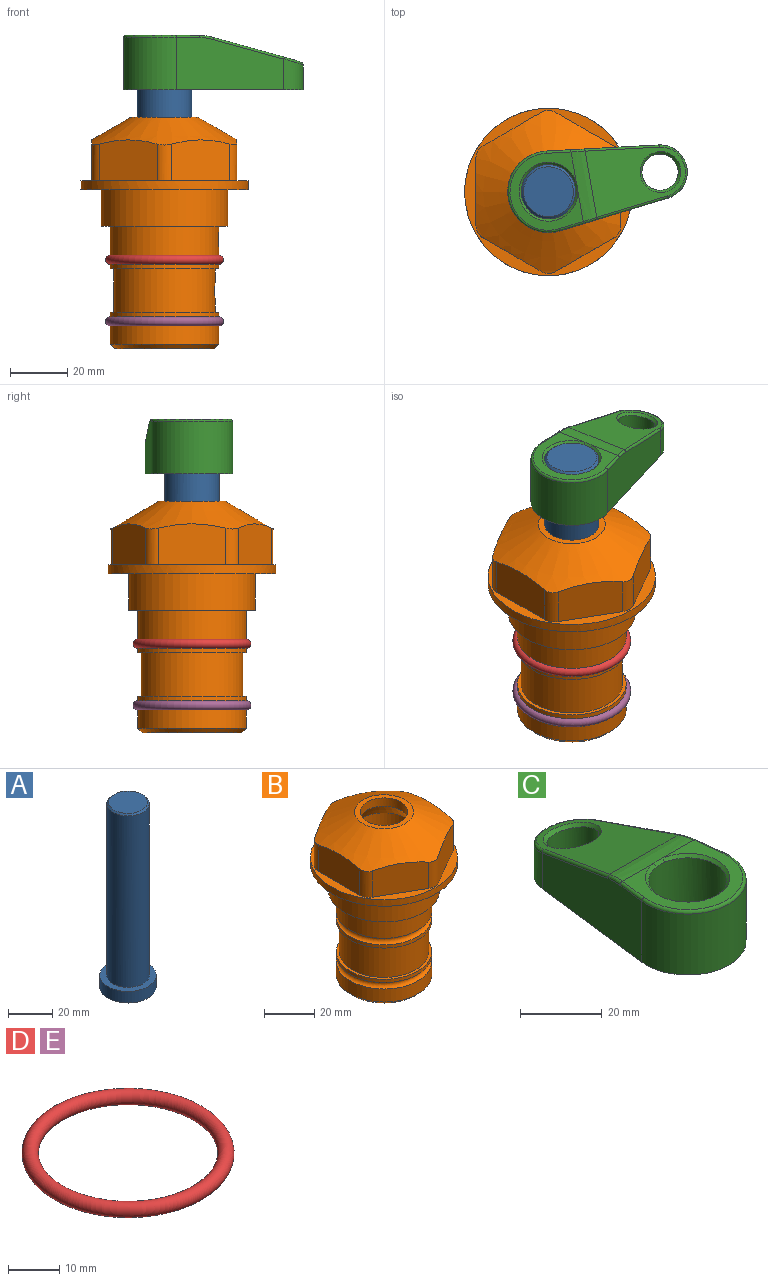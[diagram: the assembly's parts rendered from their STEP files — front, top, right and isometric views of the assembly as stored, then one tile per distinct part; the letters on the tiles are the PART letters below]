
ASSEMBLY  parts=5 mates=4
PART A: 6 faces, bbox 25.4x25.4x101.6 mm
  f0: plane 17.46x17.46mm, normal (0,0,1), area 239.5mm2, adj f5
  f1: plane 25.4x25.4mm, normal (0,0,-1), area 506.7mm2, adj f2
  f2: cylinder r=12.7mm len=25.4mm, axis (0,0,1), area 506.7mm2, adj f1,f3
  f3: plane 25.4x25.4mm, normal (0,0,1), area 221.7mm2, adj f2,f4
  f4: cylinder r=9.53mm len=94.46mm, axis (0,0,1), area 5653mm2, adj f3,f5
  f5: cone r=8.73mm half-angle=45deg, axis (0,0,-1), area 64.4mm2, adj f0,f4
PART B: 36 faces, bbox 58.7x58.7x81 mm
  f0: cylinder r=17.78mm len=35.56mm, axis (0,0,1), area 1670.8mm2, adj f23,f24,f31
  f1: cylinder r=19.05mm len=38.1mm, axis (0,0,1), area 1191.9mm2, adj f26,f27,f30
  f2: plane 58.66x58.66mm, normal (0,0,-1), area 1150.6mm2, adj f3,f28
  f3: cylinder r=29.33mm len=58.66mm, axis (0,0,-1), area 585.1mm2, adj f2,f4
  f4: plane 58.66x58.66mm, normal (0,0,1), area 475.9mm2, adj f3,f5,f6,f7,f8,f9,f10,f11
  f5: plane 20.32x14.34mm, normal (-0.5,0.87,0), area 324.4mm2, adj f4,f15,f16,f17
  f6: plane 20.32x14.34mm, normal (0.5,0.87,0), area 324.4mm2, adj f4,f14,f15,f17
  f7: plane 23.48x14.34mm, normal (1,0,0), area 324.4mm2, adj f4,f13,f14,f17
  f8: plane 20.32x14.34mm, normal (0.5,-0.87,0), area 324.4mm2, adj f4,f12,f13,f17
  f9: plane 20.32x14.34mm, normal (-0.5,-0.87,0), area 324.4mm2, adj f4,f11,f12,f17
  f10: plane 23.48x14.34mm, normal (-1,0,0), area 324.4mm2, adj f4,f11,f16,f17
  f11: cylinder r=5.08mm len=12.85mm, axis (0,0,-1), area 67.2mm2, adj f4,f9,f10,f17
  f12: cylinder r=5.08mm len=12.85mm, axis (0,0,-1), area 67.2mm2, adj f4,f8,f9,f17
  f13: cylinder r=5.08mm len=12.85mm, axis (0,0,-1), area 67.2mm2, adj f4,f7,f8,f17
  f14: cylinder r=5.08mm len=12.85mm, axis (0,0,-1), area 67.2mm2, adj f4,f6,f7,f17
  f15: cylinder r=5.08mm len=12.85mm, axis (0,0,-1), area 67.2mm2, adj f4,f5,f6,f17
  f16: cylinder r=5.08mm len=12.85mm, axis (0,0,-1), area 67.2mm2, adj f4,f5,f10,f17
  f17: cone r=11.73mm half-angle=60deg, axis (0,0,-1), area 2071.8mm2, adj f5,f6,f7,f8,f9,f10,f11,f12
  f18: plane 23.46x23.46mm, normal (0,0,1), area 147.4mm2, adj f17,f35
  f19: plane 34.93x34.93mm, normal (0,0,-1), area 958mm2, adj f29
  f20: cylinder r=19.05mm len=38.1mm, axis (0,0,1), area 760.1mm2, adj f21,f29
  f21: torus R=19.05mm, axis (0,0,1), area 565.3mm2, adj f20,f22
  f22: cylinder r=19.05mm len=38.1mm, axis (0,0,1), area 190mm2, adj f21,f23
  f23: plane 38.1x38.1mm, normal (0,0,1), area 146.9mm2, adj f0,f22
  f24: plane 38.1x38.1mm, normal (0,0,-1), area 146.9mm2, adj f0,f25
  f25: cylinder r=19.05mm len=38.1mm, axis (0,0,1), area 190mm2, adj f24,f26
  f26: torus R=19.05mm, axis (0,0,1), area 565.3mm2, adj f1,f25
  f27: plane 44.45x44.45mm, normal (0,0,-1), area 411.7mm2, adj f1,f28
  f28: cylinder r=22.23mm len=44.45mm, axis (0,0,1), area 1773.5mm2, adj f2,f27
  f29: cone r=19.05mm half-angle=45deg, axis (0,0,1), area 257.5mm2, adj f19,f20
  f30: cylinder r=3.17mm len=6.75mm, axis (-1,0,0), area 128mm2, adj f1,f33
  f31: cylinder r=3.17mm len=6.35mm, axis (-1,0,0), area 102.5mm2, adj f0,f33
  f32: plane 25.4x25.4mm, normal (0,0,1), area 506.7mm2, adj f33
  f33: cylinder r=12.7mm len=66.42mm, axis (0,0,-1), area 5236.2mm2, adj f30,f31,f32,f34
  f34: cone r=9.53mm half-angle=30deg, axis (0,0,-1), area 443.4mm2, adj f33,f35
  f35: cylinder r=9.53mm len=19.05mm, axis (0,0,-1), area 240.9mm2, adj f18,f34
PART C: 31 faces, bbox 31.7x65.5x19.8 mm
  f0: plane 39.12x18.26mm, normal (0.99,0.12,0), area 612.2mm2, adj f1,f4,f7,f11,f13,f15
  f1: cylinder r=9.53mm len=18.91mm, axis (0,0,-1), area 296.1mm2, adj f0,f2,f7,f17
  f2: plane 39.12x18.26mm, normal (-0.99,0.12,0), area 612.2mm2, adj f1,f4,f7,f12,f14,f16
  f3: cylinder r=6.35mm len=12.7mm, axis (0,0,-1), area 362.4mm2, adj f7,f18
  f4: cylinder r=14.29mm len=28.58mm, axis (0,0,-1), area 882.2mm2, adj f0,f2,f7,f10
  f5: cylinder r=9.53mm len=19.05mm, axis (0,0,-1), area 1092.6mm2, adj f7,f19,f20
  f6: plane 26.99x23.69mm, normal (0,0,1), area 216.2mm2, adj f9,f10,f11,f12,f19
  f7: plane 63.5x28.58mm, normal (0,0,-1), area 661.8mm2, adj f0,f1,f2,f3,f4,f5,f22,f23
  f8: plane 33.52x23.6mm, normal (0,0.26,0.97), area 486mm2, adj f9,f15,f16,f17,f18
  f9: cylinder r=19.05mm len=24.72mm, axis (1,0,0), area 120.4mm2, adj f6,f8,f13,f14,f20
  f10: torus R=13.49mm, axis (0,0,1), area 59mm2, adj f4,f6,f11,f12
  f11: cylinder r=0.79mm len=8.67mm, axis (0.12,-0.99,0), area 10.8mm2, adj f0,f6,f10,f13
  f12: cylinder r=0.79mm len=8.67mm, axis (0.12,0.99,0), area 10.8mm2, adj f2,f6,f10,f14
  f13: bspline ~4.95x1.42mm, area 6.1mm2, adj f0,f9,f11,f15
  f14: bspline ~4.95x1.42mm, area 6.1mm2, adj f2,f9,f12,f16
  f15: cylinder r=0.79mm len=25.95mm, axis (0.12,-0.96,0.26), area 32.9mm2, adj f0,f8,f13,f17
  f16: cylinder r=0.79mm len=25.95mm, axis (0.12,0.96,-0.26), area 32.9mm2, adj f2,f8,f14,f17
  f17: bspline ~18.91x8.38mm, area 30mm2, adj f1,f8,f15,f16
  f18: bspline ~14.29x14.29mm, area 48.3mm2, adj f3,f8
  f19: cone r=9.53mm half-angle=45deg, axis (0,0,1), area 66.5mm2, adj f5,f6,f20
  f20: bspline ~3.22x0.96mm, area 3.5mm2, adj f5,f9,f19
  f21: plane 2.75x2.72mm, normal (0,0,-1), area 2.9mm2, adj f23,f25,f28
  f22: plane 23.05x15.88mm, normal (-0.99,-0.12,0), area 323.6mm2, adj f7,f25,f26,f27,f28,f29
  f23: plane 23.05x15.88mm, normal (0.99,-0.12,0), area 323.6mm2, adj f7,f21,f25,f27,f28,f30
  f24: cylinder r=9.53mm len=10.69mm, axis (0,0,-1), area 114.7mm2, adj f7,f27,f29,f30
  f25: cylinder r=12.7mm len=20.59mm, axis (0,0,-1), area 381.1mm2, adj f7,f21,f22,f23,f26,f28
  f26: plane 2.75x2.72mm, normal (0,0,-1), area 2.9mm2, adj f22,f25,f28
  f27: plane 19.72x18.37mm, normal (0,-0.26,-0.97), area 291.8mm2, adj f22,f23,f24,f28,f29,f30
  f28: cylinder r=15.88mm len=19.92mm, axis (1,0,0), area 54.8mm2, adj f21,f22,f23,f25,f26,f27
  f29: cylinder r=1.59mm len=11mm, axis (0,0,-1), area 34.7mm2, adj f7,f22,f24,f27
  f30: cylinder r=1.59mm len=11mm, axis (0,0,-1), area 34.7mm2, adj f7,f23,f24,f27
PART D: 1 faces, bbox 44.7x44.7x3.2 mm
  f0: torus R=19.05mm, axis (0,0,1), area 1193.9mm2
PART E: same geometry as D
PLACE A rot(axis=(0,0,-1),80deg) t=(0,0,-9.4)mm
PLACE B at identity fixed
PLACE C rot(axis=(0,0,-1),80deg) t=(0,0,-9.4)mm
PLACE D at identity
PLACE E t=(0,0,-21.59)mm
MATE fastened B.f0 <-> D.f0  axis (0,0,1) through (0,0,-24.51)mm
MATE fastened E.f0 <-> B.f0  axis (0,0,1) through (0,0,-46.1)mm
MATE cylindrical A.f2 <-> B.f0  axis (0,0,-1) through (0,0,-47.5)mm
MATE fastened A.f2 <-> C.f4  axis (0,0,1) through (0,0,54.1)mm
